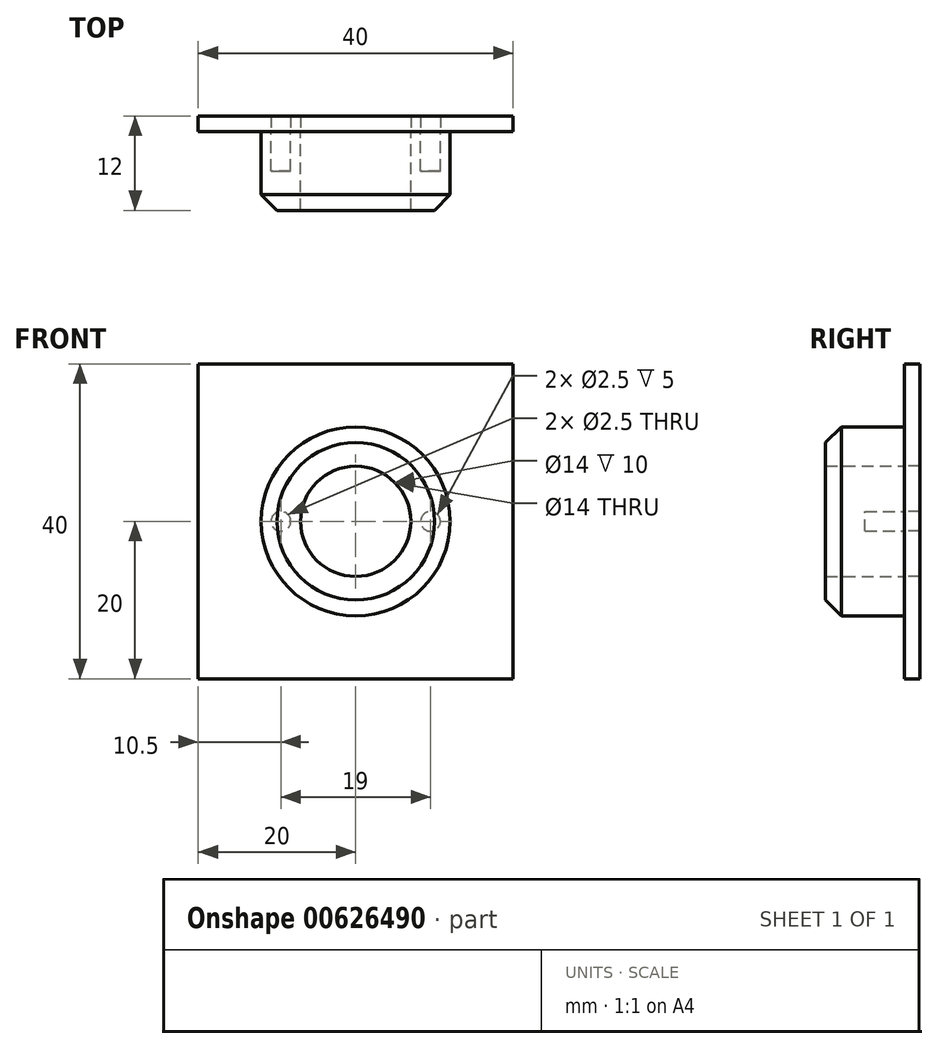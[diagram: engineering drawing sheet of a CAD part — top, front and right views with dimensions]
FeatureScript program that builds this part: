
annotation { "Feature Type Name" : "Feature", "Feature Type Description" : "" }
export const myFeature = defineFeature(function(context is Context, id is Id, definition is map)
    precondition{}
    {
        {
            var Q0;
            Q0=qCreatedBy(makeId("Front.planeOp"),FACE);
            var sketch = newSketch(context, id + "F0", { "sketchPlane" : qUnion([Q0])});
            skLineSegment(sketch, "E0.bottom", {"start": v(-20, -20) * mm, "end": v(20, -20) * mm});
            skLineSegment(sketch, "E0.top", {"start": v(-20, 20) * mm, "end": v(20, 20) * mm});
            skLineSegment(sketch, "E0.left", {"start": v(-20, -20) * mm, "end": v(-20, 20) * mm});
            skLineSegment(sketch, "E0.right", {"start": v(20, -20) * mm, "end": v(20, 20) * mm});
            skPoint(sketch, "E0.middle", {"position": v(0, 0) * mm});
            skCircle(sketch, "E1", {"center": v(0, 0) * mm, "radius": 12 * mm});
            skCircle(sketch, "E2", {"center": v(0, 0) * mm, "radius": 7 * mm});
            skPoint(sketch, "E3", {"position": v(9.5, 0) * mm});
            skLineSegment(sketch, "E4", {"start": v(7, 0) * mm, "end": v(12, 0) * mm, "construction": true});
            skPoint(sketch, "E5.MirrorP", {"position": v(-9.5, 0) * mm});
            skCircle(sketch, "E6", {"center": v(9.5, 0) * mm, "radius": 1.25 * mm});
            skCircle(sketch, "E7", {"center": v(-9.5, 0) * mm, "radius": 1.25 * mm});
            skSolve(sketch);
        }
        {
            var Q0;
            Q0 = qSketchRegion(id + "F0", true);
            var Q1;
            Q1=makeQuery(id+"F0.imprint","IMPRINT",FACE,{"disambiguationData":[TD([[makeQuery(id+"F0.imprint","IMPRINT",EDGE,{"derivedFrom":sQuery(id+"F0.wireOp",EDGE,"E1")}),1.0]])]});
            extrude(context, id + "F1", {"entities" : qUnion([Q0, Q1]), "oppositeDirection" : true, "depth" : 2 * mm, "offsetDistance" : 25 * mm});
        }
        {
            var Q0;
            Q0=makeQuery(id+"F0.imprint","IMPRINT",FACE,{"disambiguationData":[TD([[makeQuery(id+"F0.imprint","IMPRINT",EDGE,{"derivedFrom":sQuery(id+"F0.wireOp",EDGE,"E1")}),1.0]])]});
            var Q1;
            Q1=makeQuery(id+"F0.imprint","IMPRINT",FACE,{"disambiguationData":[TD([[makeQuery(id+"F0.imprint","IMPRINT",EDGE,{"derivedFrom":sQuery(id+"F0.wireOp",EDGE,"E7")}),1.0]])]});
            var Q2;
            Q2=makeQuery(id+"F0.imprint","IMPRINT",FACE,{"disambiguationData":[TD([[makeQuery(id+"F0.imprint","IMPRINT",EDGE,{"derivedFrom":sQuery(id+"F0.wireOp",EDGE,"E6")}),1.0]])]});
            extrude(context, id + "F2", {"entities" : qUnion([Q0, Q1, Q2]), "depth" : 10 * mm, "offsetDistance" : 25 * mm});
        }
        {
            var Q0;
            Q0=makeQuery(id+"F2.opExtrude","CAP_EDGE",EDGE,{"disambiguationData":[OSD([sQuery(id+"F0.wireOp",EDGE,"E1")])],"isStart":false});
            chamfer(context, id + "F3", {"entities" : qUnion([Q0]), "width" : 2 * mm, "tangentPropagation" : true});
        }
        {
            var Q0;
            Q0=makeQuery(id+"F0.imprint","IMPRINT",FACE,{"disambiguationData":[TD([[makeQuery(id+"F0.imprint","IMPRINT",EDGE,{"derivedFrom":sQuery(id+"F0.wireOp",EDGE,"E7")}),1.0]])]});
            var Q1;
            Q1=makeQuery(id+"F0.imprint","IMPRINT",FACE,{"disambiguationData":[TD([[makeQuery(id+"F0.imprint","IMPRINT",EDGE,{"derivedFrom":sQuery(id+"F0.wireOp",EDGE,"E6")}),1.0]])]});
            extrude(context, id + "F4", {"entities" : qUnion([Q0, Q1]), "operationType" : NewBodyOperationType.REMOVE, "depth" : 5 * mm, "offsetDistance" : 25 * mm});
        }
    });
